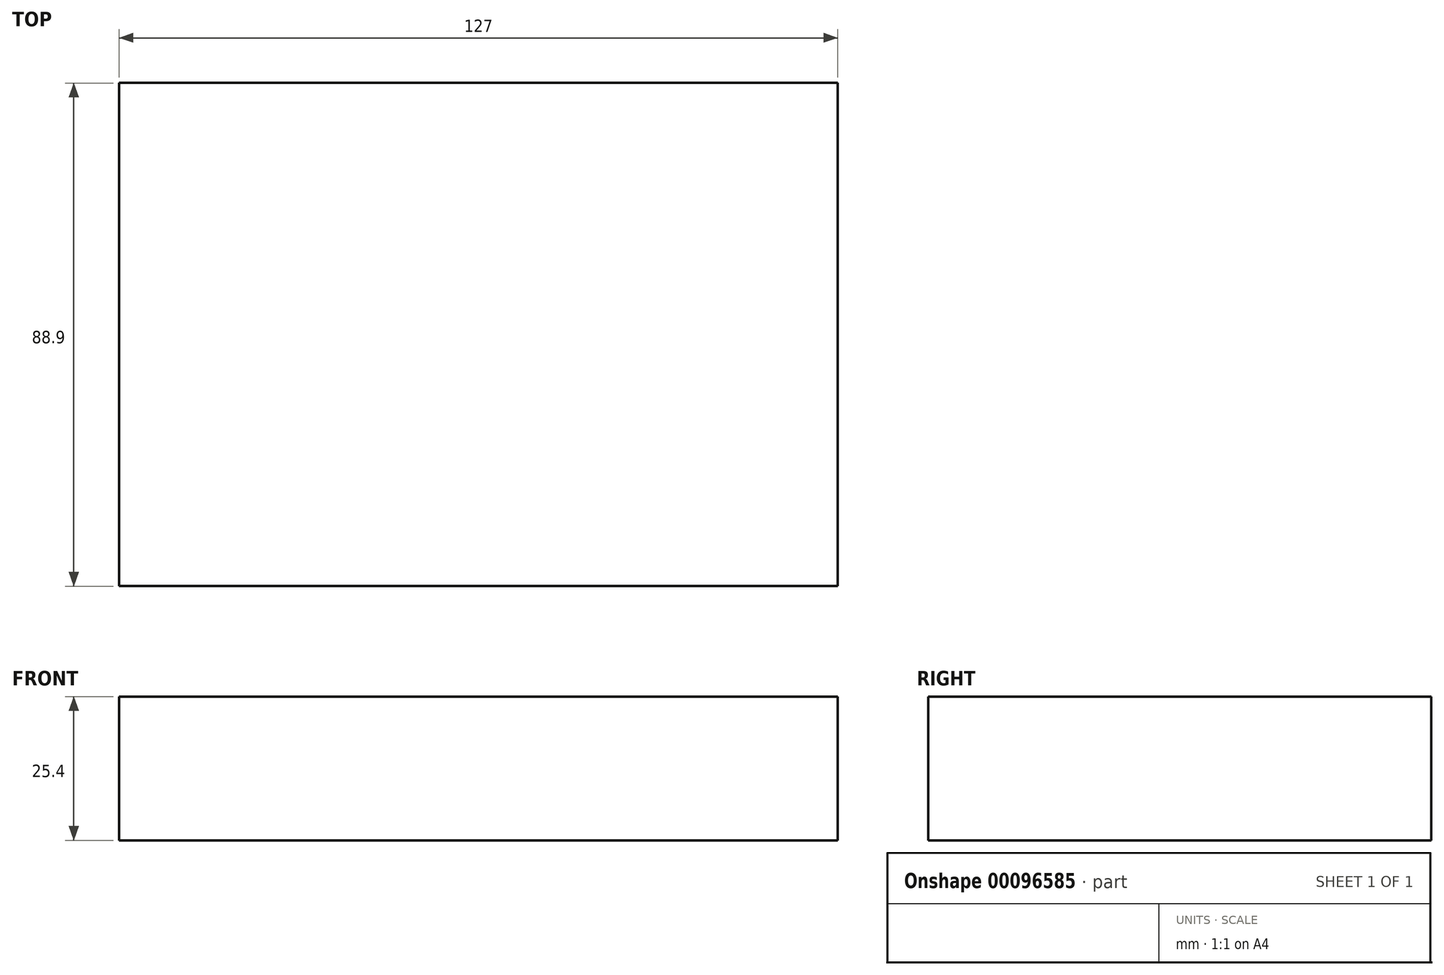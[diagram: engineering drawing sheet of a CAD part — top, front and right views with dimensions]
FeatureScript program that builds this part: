
annotation { "Feature Type Name" : "Feature", "Feature Type Description" : "" }
export const myFeature = defineFeature(function(context is Context, id is Id, definition is map)
    precondition{}
    {
        {
            var Q0;
            Q0=qCreatedBy(makeId("Top.planeOp"),FACE);
            var sketch = newSketch(context, id + "F0", { "sketchPlane" : qUnion([Q0])});
            skLineSegment(sketch, "E0", {"start": v(105.84, 43.9) * mm, "end": v(-21.16, 43.9) * mm});
            skLineSegment(sketch, "E1", {"start": v(-21.16, 43.9) * mm, "end": v(-21.16, -45) * mm});
            skLineSegment(sketch, "E2", {"start": v(-21.16, -45) * mm, "end": v(105.84, -45) * mm});
            skLineSegment(sketch, "E3", {"start": v(105.84, -45) * mm, "end": v(105.84, 43.9) * mm});
            skSolve(sketch);
        }
        {
            var Q0;
            Q0=makeQuery(id+"F0.imprint","IMPRINT",FACE,{"disambiguationData":[TD([[makeQuery(id+"F0.imprint","IMPRINT",EDGE,{"derivedFrom":sQuery(id+"F0.wireOp",EDGE,"E0")}),1.0]])]});
            extrude(context, id + "F1", {"entities" : qUnion([Q0]), "depth" : 25.4 * mm});
        }
    });
